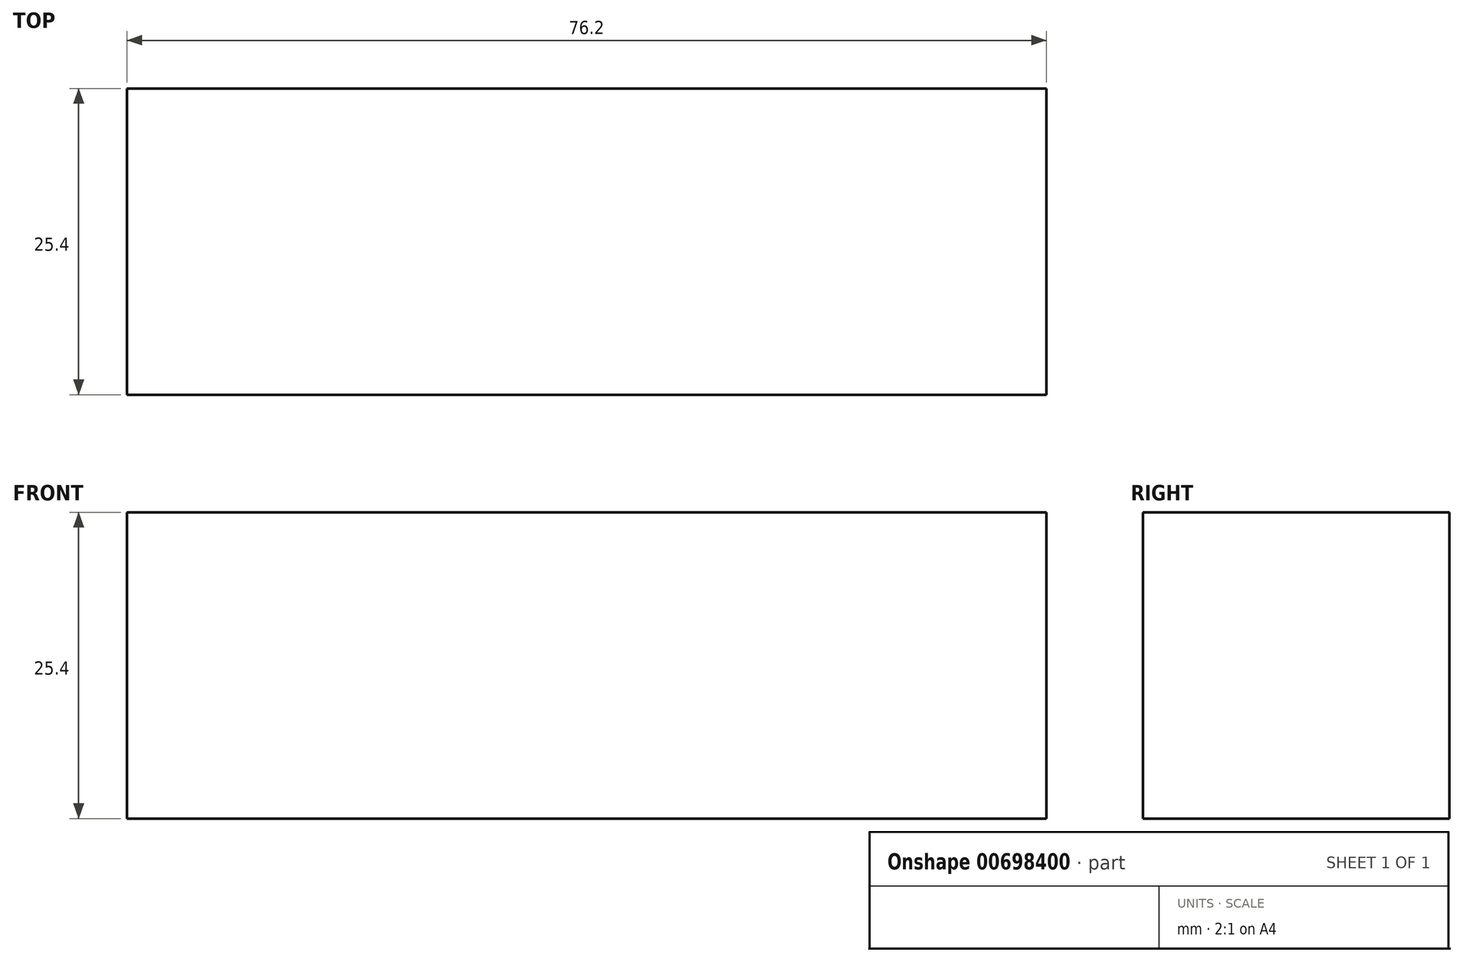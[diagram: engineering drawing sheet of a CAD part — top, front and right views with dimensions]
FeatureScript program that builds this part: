
annotation { "Feature Type Name" : "Feature", "Feature Type Description" : "" }
export const myFeature = defineFeature(function(context is Context, id is Id, definition is map)
    precondition{}
    {
        {
            var Q0;
            Q0=qCreatedBy(makeId("Front.planeOp"),FACE);
            var sketch = newSketch(context, id + "F0", { "sketchPlane" : qUnion([Q0])});
            skLineSegment(sketch, "E0.bottom", {"start": v(-25.4, 25.4) * mm, "end": v(0, 25.4) * mm});
            skLineSegment(sketch, "E0.top", {"start": v(-25.4, 0) * mm, "end": v(0, 0) * mm});
            skLineSegment(sketch, "E0.left", {"start": v(-25.4, 25.4) * mm, "end": v(-25.4, 0) * mm});
            skLineSegment(sketch, "E0.right", {"start": v(0, 25.4) * mm, "end": v(0, 0) * mm});
            skLineSegment(sketch, "E1.bottom", {"start": v(0, 25.4) * mm, "end": v(25.4, 25.4) * mm});
            skLineSegment(sketch, "E1.top", {"start": v(0, 0) * mm, "end": v(25.4, 0) * mm});
            skLineSegment(sketch, "E1.right", {"start": v(25.4, 25.4) * mm, "end": v(25.4, 0) * mm});
            skLineSegment(sketch, "E2.bottom", {"start": v(25.4, 25.4) * mm, "end": v(50.8, 25.4) * mm});
            skLineSegment(sketch, "E2.top", {"start": v(25.4, 0) * mm, "end": v(50.8, 0) * mm});
            skLineSegment(sketch, "E2.right", {"start": v(50.8, 25.4) * mm, "end": v(50.8, 0) * mm});
            skLineSegment(sketch, "E3.bottom", {"start": v(25.4, 25.4) * mm, "end": v(0, 25.4) * mm});
            skLineSegment(sketch, "E3.top", {"start": v(25.4, 50.8) * mm, "end": v(0, 50.8) * mm});
            skLineSegment(sketch, "E3.left", {"start": v(25.4, 25.4) * mm, "end": v(25.4, 50.8) * mm});
            skLineSegment(sketch, "E3.right", {"start": v(0, 25.4) * mm, "end": v(0, 50.8) * mm});
            skSolve(sketch);
        }
        {
            var Q0;
            Q0=makeQuery(id+"F0.imprint","IMPRINT",FACE,{"disambiguationData":[TD([[makeQuery(id+"F0.imprint","IMPRINT",EDGE,{"derivedFrom":sQuery(id+"F0.wireOp",EDGE,"E0.bottom")}),-1.0]])]});
            var Q1;
            Q1=makeQuery(id+"F0.imprint","IMPRINT",FACE,{"disambiguationData":[TD([[makeQuery(id+"F0.imprint","IMPRINT",EDGE,{"derivedFrom":sQuery(id+"F0.wireOp",EDGE,"E3.bottom")}),-1.0]])]});
            var Q2;
            Q2=makeQuery(id+"F0.imprint","IMPRINT",FACE,{"disambiguationData":[TD([[makeQuery(id+"F0.imprint","IMPRINT",EDGE,{"derivedFrom":sQuery(id+"F0.wireOp",EDGE,"E1.top")}),1.0]])]});
            var Q3;
            Q3=makeQuery(id+"F0.imprint","IMPRINT",FACE,{"disambiguationData":[TD([[makeQuery(id+"F0.imprint","IMPRINT",EDGE,{"derivedFrom":sQuery(id+"F0.wireOp",EDGE,"E2.bottom")}),-1.0]])]});
            extrude(context, id + "F1", {"entities" : qUnion([Q0, Q1, Q2, Q3]), "depth" : 25.4 * mm, "offsetDistance" : 25.4 * mm});
        }
    });
